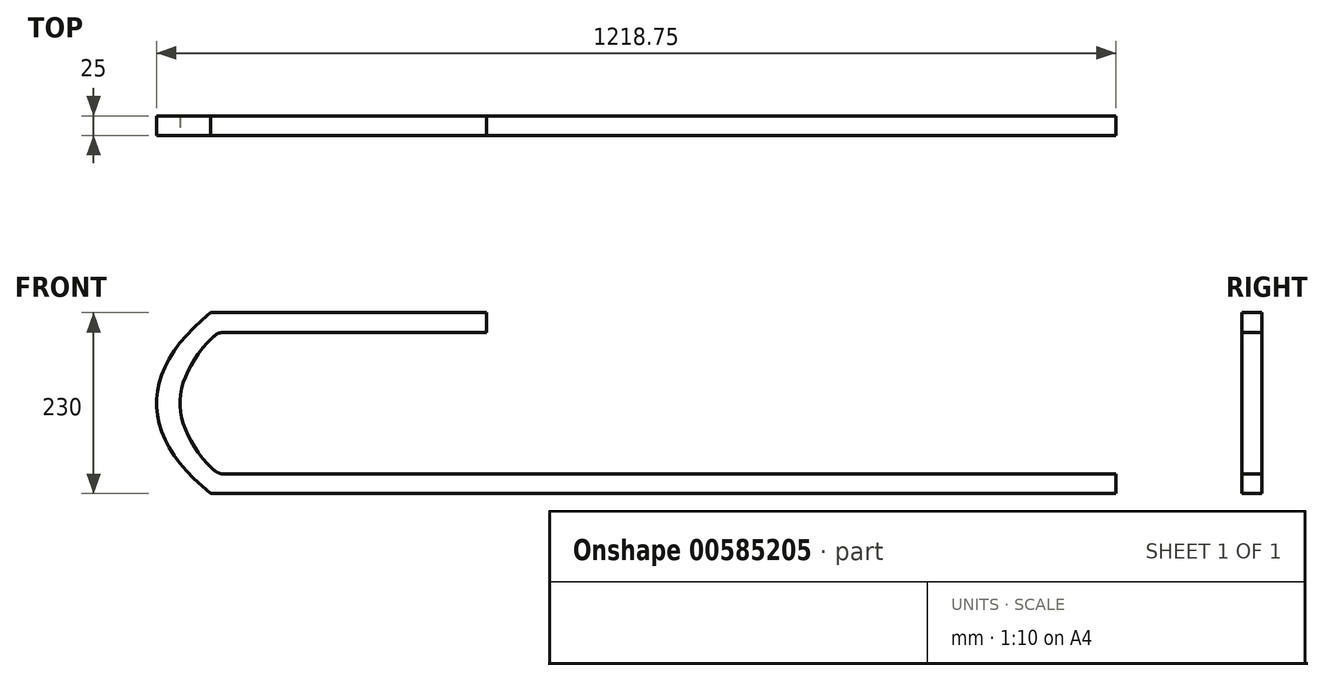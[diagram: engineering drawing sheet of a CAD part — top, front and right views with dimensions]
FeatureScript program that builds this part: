
annotation { "Feature Type Name" : "Feature", "Feature Type Description" : "" }
export const myFeature = defineFeature(function(context is Context, id is Id, definition is map)
    precondition{}
    {
        {
            var Q0;
            Q0=qCreatedBy(makeId("Front.planeOp"),FACE);
            var sketch = newSketch(context, id + "F0", { "sketchPlane" : qUnion([Q0])});
            skLineSegment(sketch, "E0", {"start": v(0, 0) * mm, "end": v(1150, 0) * mm});
            skLineSegment(sketch, "E1", {"start": v(1150, 25) * mm, "end": v(1150, 0) * mm});
            skLineSegment(sketch, "E2", {"start": v(1150, 25) * mm, "end": v(9.16, 25) * mm});
            skEllipticalArc(sketch, "E3", {});
            skEllipticalArc(sketch, "E4", {});
            skLineSegment(sketch, "E5", {"start": v(831.25, 115) * mm, "end": v(-68.75, 115) * mm, "construction": true});
            skLineSegment(sketch, "E6", {"start": v(-38.75, 115) * mm, "end": v(-68.75, 115) * mm, "construction": true});
            skLineSegment(sketch, "E7", {"start": v(831.25, 115) * mm, "end": v(831.25, -185) * mm, "construction": true});
            skLineSegment(sketch, "E8", {"start": v(831.25, -160) * mm, "end": v(831.25, -185) * mm, "construction": true});
            skLineSegment(sketch, "E9", {"start": v(0, 0) * mm, "end": v(0, 115) * mm, "construction": true});
            skLineSegment(sketch, "E10", {"start": v(0, 115) * mm, "end": v(0, 230) * mm, "construction": true});
            skLineSegment(sketch, "E11", {"start": v(0, 230) * mm, "end": v(350, 230) * mm});
            skLineSegment(sketch, "E12", {"start": v(350, 205) * mm, "end": v(350, 230) * mm});
            skLineSegment(sketch, "E13", {"start": v(350, 205) * mm, "end": v(9.16, 205) * mm});
            const initialGuessF0  = {"E3": [0.8312490601498446, 0.115, -1, 0, 0.9, 0.3, 5.889782675169492, 0.39340263201009495], "E4": [0.8312490601498446, 0.115, -1, 0, 0.87, 0.275, 5.9497693969706305, 0.3334159102089561]};
            skSetInitialGuess(sketch, initialGuessF0);
            skSolve(sketch);
        }
        {
            var Q0;
            {var subQ4=sQuery(id+"F0.wireOp",EDGE,"E12");Q0=makeQuery(id+"F0.imprint","IMPRINT",FACE,{"disambiguationData":[TD([[makeQuery(id+"F0.imprint","IMPRINT",EDGE,{"derivedFrom":subQ4}),1.0]])]});}
            var Q1;
            {var subQ5=sQuery(id+"F0.wireOp",EDGE,"E0");var subQ7=sQuery(id+"F0.wireOp",EDGE,"E3");var subQ8=makeQuery(id+"F0.imprint","INTERSECT",VERTEX,{"derivedFrom":[subQ5,subQ7]});Q1=makeQuery(id+"F0.imprint","IMPRINT",FACE,{"disambiguationData":[TD([[makeQuery(id+"F0.imprint","IMPRINT",EDGE,{"disambiguationData":[TD([[subQ8,-1.0]])],"derivedFrom":subQ5}),1.0]])]});}
            var Q2;
            {var subQ0=sQuery(id+"F0.wireOp",EDGE,"E1");Q2=makeQuery(id+"F0.imprint","IMPRINT",FACE,{"disambiguationData":[TD([[makeQuery(id+"F0.imprint","IMPRINT",EDGE,{"derivedFrom":subQ0}),-1.0]])]});}
            extrude(context, id + "F1", {"entities" : qUnion([Q0, Q1, Q2]), "endBound" : BoundingType.SYMMETRIC, "depth" : 25 * mm, "offsetDistance" : 25 * mm});
        }
        {
            var Q0;
            Q0=makeQuery(id+"F1.opExtrude","SWEPT_EDGE",EDGE,{"disambiguationData":[OSD([sQuery(id+"F0.wireOp",EDGE,"E2"),sQuery(id+"F0.wireOp",EDGE,"E4")])]});
            var Q1;
            Q1=makeQuery(id+"F1.opExtrude","SWEPT_EDGE",EDGE,{"disambiguationData":[OSD([sQuery(id+"F0.wireOp",EDGE,"E4"),sQuery(id+"F0.wireOp",EDGE,"E13")])]});
            fillet(context, id + "F2", {"entities" : qUnion([Q0, Q1]), "radius" : 20 * mm, "tangentPropagation" : true, "allowEdgeOverflow" : false});
        }
    });
